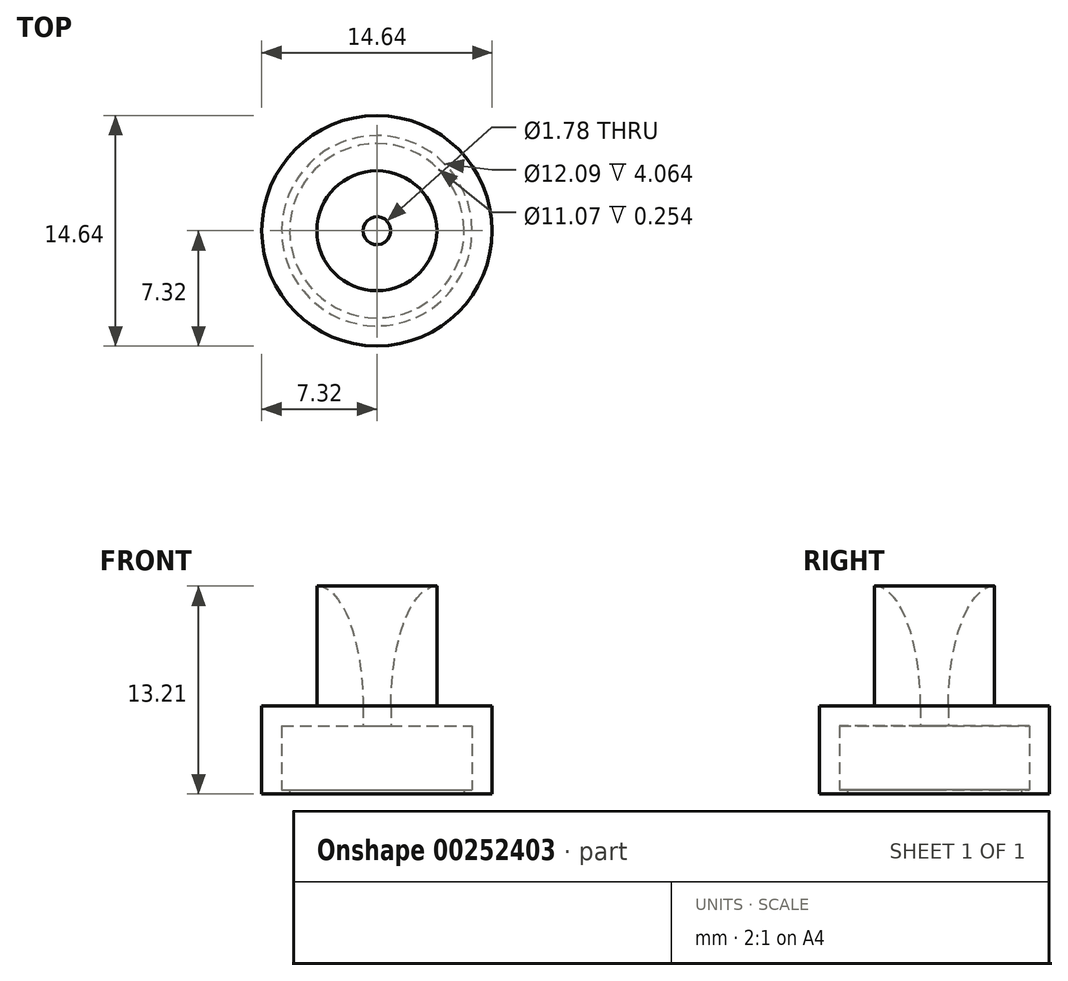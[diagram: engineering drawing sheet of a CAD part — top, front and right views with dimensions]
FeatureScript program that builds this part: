
annotation { "Feature Type Name" : "Feature", "Feature Type Description" : "" }
export const myFeature = defineFeature(function(context is Context, id is Id, definition is map)
    precondition{}
    {
        {
            var Q0;
            Q0=qCreatedBy(makeId("Front.planeOp"),FACE);
            var sketch = newSketch(context, id + "F0", { "sketchPlane" : qUnion([Q0])});
            skPoint(sketch, "E0.endSnap0", {"position": v(3.81, 7.62) * mm});
            skLineSegment(sketch, "E1", {"start": v(3.8, 7.62) * mm, "end": v(3.81, 0) * mm});
            skPoint(sketch, "E2", {"position": v(0.89, 0) * mm});
            skLineSegment(sketch, "E3", {"start": v(0.89, 0) * mm, "end": v(3.81, 0) * mm});
            skLineSegment(sketch, "E4", {"start": v(0, 0) * mm, "end": v(0, 17.12) * mm, "construction": true});
            skEllipticalArc(sketch, "E5", {});
            skLineSegment(sketch, "E6.bottom", {"start": v(0.89, 0) * mm, "end": v(7.32, 0) * mm});
            skLineSegment(sketch, "E6.top", {"start": v(0.89, -1.27) * mm, "end": v(6.05, -1.27) * mm});
            skLineSegment(sketch, "E6.left", {"start": v(0.89, 0) * mm, "end": v(0.89, -1.27) * mm});
            skLineSegment(sketch, "E7.top", {"start": v(7.32, -5.33) * mm, "end": v(6.05, -5.33) * mm});
            skLineSegment(sketch, "E7.left", {"start": v(7.32, 0) * mm, "end": v(7.32, -5.33) * mm});
            skLineSegment(sketch, "E7.right", {"start": v(6.05, -1.27) * mm, "end": v(6.05, -5.33) * mm});
            skLineSegment(sketch, "E8.bottom", {"start": v(7.32, -5.33) * mm, "end": v(5.54, -5.33) * mm});
            skLineSegment(sketch, "E8.top", {"start": v(7.32, -5.59) * mm, "end": v(5.54, -5.59) * mm});
            skLineSegment(sketch, "E8.left", {"start": v(7.32, -5.33) * mm, "end": v(7.32, -5.59) * mm});
            skLineSegment(sketch, "E8.right", {"start": v(5.54, -5.33) * mm, "end": v(5.54, -5.59) * mm});
            const initialGuessF0  = {"E5": [0.00381, 0, 0, 1, 0.00762, 0.002921, 0, 1.5707963267948966]};
            skSetInitialGuess(sketch, initialGuessF0);
            skSolve(sketch);
        }
        {
            var Q0;
            {var subQ0=sQuery(id+"F0.wireOp",EDGE,"E1");Q0=makeQuery(id+"F0.imprint","IMPRINT",FACE,{"disambiguationData":[TD([[makeQuery(id+"F0.imprint","IMPRINT",EDGE,{"derivedFrom":subQ0}),-1.0]])]});}
            var Q1;
            Q1=makeQuery(id+"F0.imprint","IMPRINT",FACE,{"disambiguationData":[TD([[makeQuery(id+"F0.imprint","IMPRINT",EDGE,{"derivedFrom":sQuery(id+"F0.wireOp",EDGE,"E6.top")}),1.0]])]});
            var Q2;
            Q2=makeQuery(id+"F0.imprint","IMPRINT",FACE,{"disambiguationData":[TD([[makeQuery(id+"F0.imprint","IMPRINT",EDGE,{"derivedFrom":sQuery(id+"F0.wireOp",EDGE,"E8.top")}),-1.0]])]});
            var Q3;
            Q3=sQuery(id+"F0.wireOp",EDGE,"E4");
            revolve(context, id + "F1", {"entities" : qUnion([Q0, Q1, Q2]), "axis" : qUnion([Q3]), "revolveType" : RevolveType.FULL});
        }
    });
